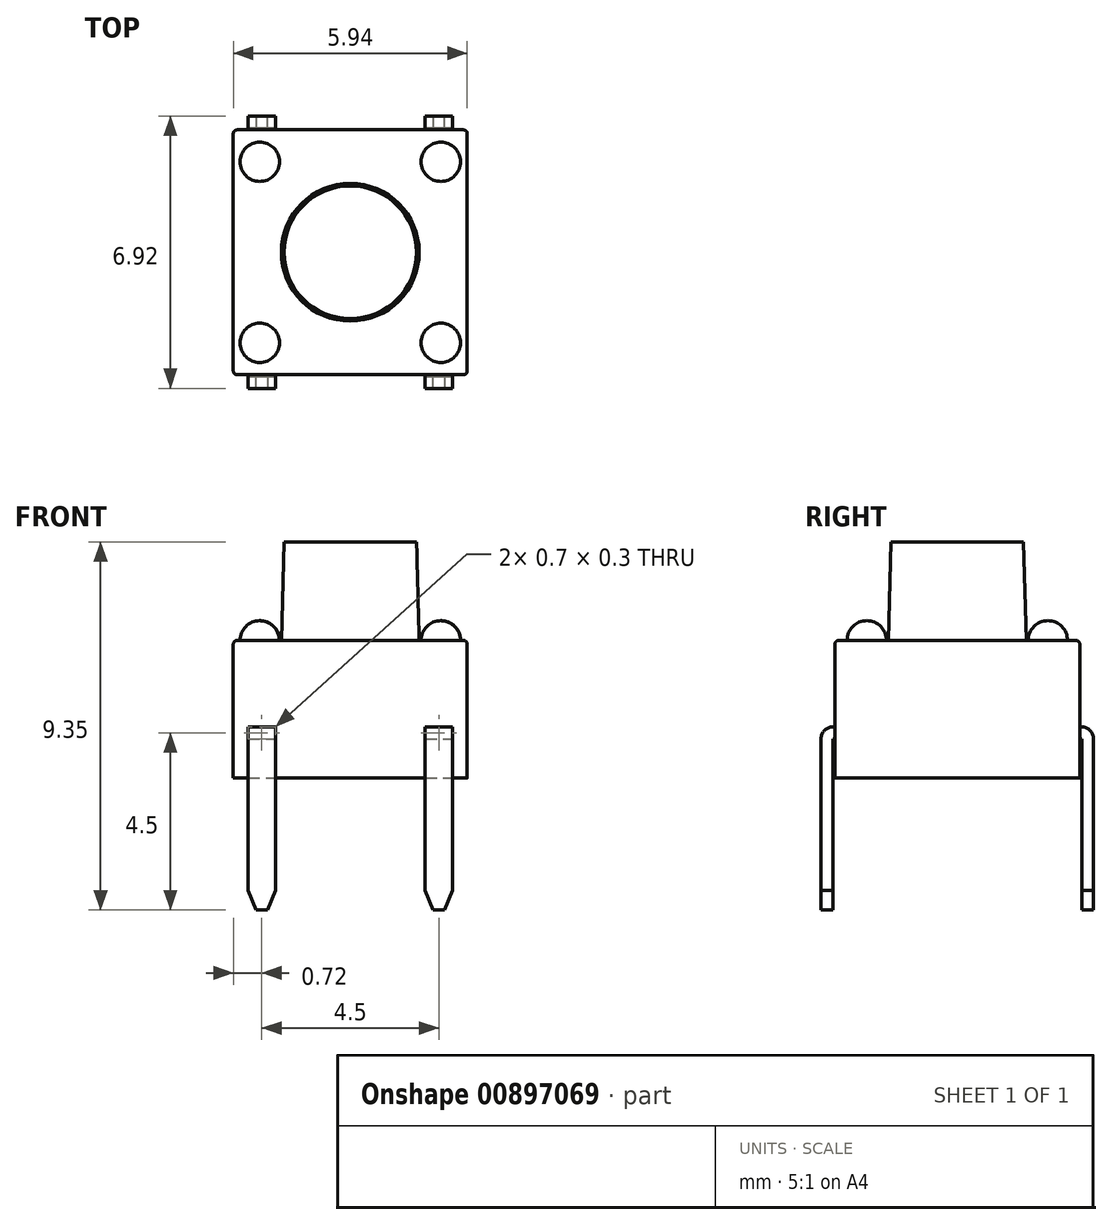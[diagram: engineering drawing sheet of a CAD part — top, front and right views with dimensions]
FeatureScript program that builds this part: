
annotation { "Feature Type Name" : "Feature", "Feature Type Description" : "" }
export const myFeature = defineFeature(function(context is Context, id is Id, definition is map)
    precondition{}
    {
        {
            var Q0;
            Q0=qCreatedBy(makeId("Top.planeOp"),FACE);
            var sketch = newSketch(context, id + "F0", { "sketchPlane" : qUnion([Q0])});
            skLineSegment(sketch, "E0.bottom", {"start": v(-2.97, 3.11) * mm, "end": v(2.97, 3.11) * mm});
            skLineSegment(sketch, "E0.top", {"start": v(-2.97, -3.11) * mm, "end": v(2.97, -3.11) * mm});
            skLineSegment(sketch, "E0.left", {"start": v(-2.97, 3.11) * mm, "end": v(-2.97, -3.11) * mm});
            skLineSegment(sketch, "E0.right", {"start": v(2.97, 3.11) * mm, "end": v(2.97, -3.11) * mm});
            skSolve(sketch);
        }
        {
            var Q0;
            Q0=makeQuery(id+"F0.imprint","IMPRINT",FACE,{"disambiguationData":[TD([[makeQuery(id+"F0.imprint","IMPRINT",EDGE,{"derivedFrom":sQuery(id+"F0.wireOp",EDGE,"E0.bottom")}),-1.0]])]});
            extrude(context, id + "F1", {"entities" : qUnion([Q0]), "depth" : 3.5 * mm});
        }
        {
            var Q0;
            Q0=makeQuery(id+"F1.opExtrude","CAP_FACE",FACE,{"disambiguationData":[OSD([sQuery(id+"F0.wireOp",EDGE,"E0.bottom"),sQuery(id+"F0.wireOp",EDGE,"E0.top"),sQuery(id+"F0.wireOp",EDGE,"E0.left"),sQuery(id+"F0.wireOp",EDGE,"E0.right")])],"isStart":false});
            var sketch = newSketch(context, id + "F2", { "sketchPlane" : qUnion([Q0])});
            skCircle(sketch, "E1", {"center": v(0, 0) * mm, "radius": 1.75 * mm});
            skSolve(sketch);
        }
        {
            var Q0;
            Q0=qSketchRegion(id+"F2",true);
            extrude(context, id + "F3", {"entities" : qUnion([Q0]), "operationType" : NewBodyOperationType.ADD, "offsetDistance" : 25 * mm, "depth" : 2.5 * mm, "hasDraft" : true, "draftAngle" : 1.5 * degree, "draftPullDirection" : true});
        }
        {
            var Q0;
            Q0=makeQuery(id+"F1.opExtrude","SWEPT_EDGE",EDGE,{"disambiguationData":[OSD([sQuery(id+"F0.wireOp",EDGE,"E0.top"),sQuery(id+"F0.wireOp",EDGE,"E0.right")])]});
            var Q1;
            Q1=makeQuery(id+"F1.opExtrude","SWEPT_EDGE",EDGE,{"disambiguationData":[OSD([sQuery(id+"F0.wireOp",EDGE,"E0.top"),sQuery(id+"F0.wireOp",EDGE,"E0.left")])]});
            var Q2;
            Q2=makeQuery(id+"F1.opExtrude","SWEPT_EDGE",EDGE,{"disambiguationData":[OSD([sQuery(id+"F0.wireOp",EDGE,"E0.bottom"),sQuery(id+"F0.wireOp",EDGE,"E0.left")])]});
            var Q3;
            Q3=makeQuery(id+"F1.opExtrude","SWEPT_EDGE",EDGE,{"disambiguationData":[OSD([sQuery(id+"F0.wireOp",EDGE,"E0.bottom"),sQuery(id+"F0.wireOp",EDGE,"E0.right")])]});
            var Q4;
            Q4=makeQuery(id+"F1.opExtrude","CAP_EDGE",EDGE,{"disambiguationData":[OSD([sQuery(id+"F0.wireOp",EDGE,"E0.right")])],"isStart":false});
            var Q5;
            Q5=makeQuery(id+"F1.opExtrude","CAP_EDGE",EDGE,{"disambiguationData":[OSD([sQuery(id+"F0.wireOp",EDGE,"E0.top")])],"isStart":false});
            var Q6;
            Q6=makeQuery(id+"F1.opExtrude","CAP_EDGE",EDGE,{"disambiguationData":[OSD([sQuery(id+"F0.wireOp",EDGE,"E0.left")])],"isStart":false});
            var Q7;
            Q7=makeQuery(id+"F1.opExtrude","CAP_EDGE",EDGE,{"disambiguationData":[OSD([sQuery(id+"F0.wireOp",EDGE,"E0.bottom")])],"isStart":false});
            fillet(context, id + "F4", {"entities" : qUnion([Q0, Q1, Q2, Q3, Q4, Q5, Q6, Q7]), "radius" : 0.1 * mm, "tangentPropagation" : true, "allowEdgeOverflow" : false});
        }
        {
            var Q0;
            Q0=makeQuery(id+"F1.opExtrude","CAP_FACE",FACE,{"disambiguationData":[OSD([sQuery(id+"F0.wireOp",EDGE,"E0.bottom"),sQuery(id+"F0.wireOp",EDGE,"E0.top"),sQuery(id+"F0.wireOp",EDGE,"E0.left"),sQuery(id+"F0.wireOp",EDGE,"E0.right")])],"isStart":false});
            var sketch = newSketch(context, id + "F5", { "sketchPlane" : qUnion([Q0])});
            skCircle(sketch, "E2", {"center": v(2.3, 2.3) * mm, "radius": 0.5 * mm});
            skCircle(sketch, "E3", {"center": v(2.3, -2.3) * mm, "radius": 0.5 * mm});
            skCircle(sketch, "E4", {"center": v(-2.3, -2.3) * mm, "radius": 0.5 * mm});
            skCircle(sketch, "E5", {"center": v(-2.3, 2.3) * mm, "radius": 0.5 * mm});
            skLineSegment(sketch, "E6", {"start": v(0, -3.01) * mm, "end": v(0, 3.01) * mm, "construction": true});
            skLineSegment(sketch, "E7", {"start": v(2.87, 0) * mm, "end": v(-2.87, 0) * mm, "construction": true});
            skSolve(sketch);
        }
        {
            var Q0;
            Q0=makeQuery(id+"F5.imprint","IMPRINT",FACE,{"disambiguationData":[TD([[makeQuery(id+"F5.imprint","IMPRINT",EDGE,{"derivedFrom":sQuery(id+"F5.wireOp",EDGE,"E3")}),1.0]])]});
            var Q1;
            Q1=makeQuery(id+"F5.imprint","IMPRINT",FACE,{"disambiguationData":[TD([[makeQuery(id+"F5.imprint","IMPRINT",EDGE,{"derivedFrom":sQuery(id+"F5.wireOp",EDGE,"E2")}),1.0]])]});
            var Q2;
            Q2=makeQuery(id+"F5.imprint","IMPRINT",FACE,{"disambiguationData":[TD([[makeQuery(id+"F5.imprint","IMPRINT",EDGE,{"derivedFrom":sQuery(id+"F5.wireOp",EDGE,"E5")}),1.0]])]});
            var Q3;
            Q3=makeQuery(id+"F5.imprint","IMPRINT",FACE,{"disambiguationData":[TD([[makeQuery(id+"F5.imprint","IMPRINT",EDGE,{"derivedFrom":sQuery(id+"F5.wireOp",EDGE,"E4")}),1.0]])]});
            extrude(context, id + "F6", {"entities" : qUnion([Q0, Q1, Q2, Q3]), "operationType" : NewBodyOperationType.ADD, "offsetDistance" : 25 * mm, "depth" : 0.5 * mm});
        }
        {
            var Q0;
            Q0=makeQuery(id+"F6.opExtrude","CAP_EDGE",EDGE,{"disambiguationData":[OSD([sQuery(id+"F5.wireOp",EDGE,"E3")])],"isStart":false});
            var Q1;
            Q1=makeQuery(id+"F6.opExtrude","CAP_EDGE",EDGE,{"disambiguationData":[OSD([sQuery(id+"F5.wireOp",EDGE,"E2")])],"isStart":false});
            var Q2;
            Q2=makeQuery(id+"F6.opExtrude","CAP_EDGE",EDGE,{"disambiguationData":[OSD([sQuery(id+"F5.wireOp",EDGE,"E5")])],"isStart":false});
            var Q3;
            Q3=makeQuery(id+"F6.opExtrude","CAP_EDGE",EDGE,{"disambiguationData":[OSD([sQuery(id+"F5.wireOp",EDGE,"E4")])],"isStart":false});
            fillet(context, id + "F7", {"entities" : qUnion([Q0, Q1, Q2, Q3]), "radius" : 0.5 * mm, "tangentPropagation" : true, "allowEdgeOverflow" : false});
        }
        {
            var Q0;
            Q0=makeQuery(id+"F1.opExtrude","SWEPT_FACE",FACE,{"disambiguationData":[OSD([sQuery(id+"F0.wireOp",EDGE,"E0.top")])]});
            var sketch = newSketch(context, id + "F8", { "sketchPlane" : qUnion([Q0])});
            skLineSegment(sketch, "E8.bottom", {"start": v(-2.6, 1.3) * mm, "end": v(-1.9, 1.3) * mm});
            skLineSegment(sketch, "E8.top", {"start": v(-2.6, 1) * mm, "end": v(-1.9, 1) * mm});
            skLineSegment(sketch, "E8.left", {"start": v(-2.6, 1.3) * mm, "end": v(-2.6, 1) * mm});
            skLineSegment(sketch, "E8.right", {"start": v(-1.9, 1.3) * mm, "end": v(-1.9, 1) * mm});
            skLineSegment(sketch, "E9.bottom", {"start": v(1.9, 1.3) * mm, "end": v(2.6, 1.3) * mm});
            skLineSegment(sketch, "E9.top", {"start": v(1.9, 1) * mm, "end": v(2.6, 1) * mm});
            skLineSegment(sketch, "E9.left", {"start": v(1.9, 1.3) * mm, "end": v(1.9, 1) * mm});
            skLineSegment(sketch, "E9.right", {"start": v(2.6, 1.3) * mm, "end": v(2.6, 1) * mm});
            skLineSegment(sketch, "E10", {"start": v(0, 3.4) * mm, "end": v(0, 0) * mm, "construction": true});
            skSolve(sketch);
        }
        {
            var Q0;
            Q0=qCreatedBy(makeId("Right.planeOp"),FACE);
            var sketch = newSketch(context, id + "F9", { "sketchPlane" : qUnion([Q0])});
            skLineSegment(sketch, "E11", {"start": v(-3.11, 1.15) * mm, "end": v(-3.16, 1.15) * mm});
            skLineSegment(sketch, "E12", {"start": v(-3.11, 1.58) * mm, "end": v(-3.11, 0.7) * mm, "construction": true});
            skLineSegment(sketch, "E13", {"start": v(-3.31, 1) * mm, "end": v(-3.31, -3.35) * mm});
            skPoint(sketch, "E14.visualSharp", {"position": v(-3.31, 1.15) * mm});
            skArc(sketch, "E14.filletArc", {"start": v(-3.16, 1.15) * mm, "mid": v(-3.27, 1.1) * mm, "end": v(-3.31, 1) * mm});
            skSolve(sketch);
        }
        {
            var Q0;
            Q0=makeQuery(id+"F8.imprint","IMPRINT",FACE,{"disambiguationData":[TD([[makeQuery(id+"F8.imprint","IMPRINT",EDGE,{"derivedFrom":sQuery(id+"F8.wireOp",EDGE,"E8.bottom")}),-1.0]])]});
            var Q1;
            Q1=makeQuery(id+"F8.imprint","IMPRINT",FACE,{"disambiguationData":[TD([[makeQuery(id+"F8.imprint","IMPRINT",EDGE,{"derivedFrom":sQuery(id+"F8.wireOp",EDGE,"E9.bottom")}),-1.0]])]});
            var Q2;
            Q2=sQuery(id+"F9.wireOp",EDGE,"E11");
            var Q3;
            Q3=sQuery(id+"F9.wireOp",EDGE,"E14.filletArc");
            var Q4;
            Q4=sQuery(id+"F9.wireOp",EDGE,"E13");
            sweep(context, id + "F10", {"profiles" : qUnion([Q0, Q1]), "path" : qUnion([Q2, Q3, Q4])});
        }
        {
            var Q0;
            Q0=makeQuery(id+"F10.opSweep","CAP_EDGE",EDGE,{"disambiguationData":[OSD([sQuery(id+"F8.wireOp",EDGE,"E8.left"),sQuery(id+"F9.wireOp",VERTEX,"E13.end")])],"isStart":false});
            var Q1;
            Q1=makeQuery(id+"F10.opSweep","CAP_EDGE",EDGE,{"disambiguationData":[OSD([sQuery(id+"F8.wireOp",EDGE,"E8.right"),sQuery(id+"F9.wireOp",VERTEX,"E13.end")])],"isStart":false});
            var Q2;
            Q2=makeQuery(id+"F10.opSweep","CAP_EDGE",EDGE,{"disambiguationData":[OSD([sQuery(id+"F8.wireOp",EDGE,"E9.left"),sQuery(id+"F9.wireOp",VERTEX,"E13.end")])],"isStart":false});
            var Q3;
            Q3=makeQuery(id+"F10.opSweep","CAP_EDGE",EDGE,{"disambiguationData":[OSD([sQuery(id+"F8.wireOp",EDGE,"E9.right"),sQuery(id+"F9.wireOp",VERTEX,"E13.end")])],"isStart":false});
            chamfer(context, id + "F11", {"entities" : qUnion([Q0, Q1, Q2, Q3]), "chamferType" : ChamferType.TWO_OFFSETS, "width1" : 0.2 * mm, "oppositeDirection" : false, "width2" : 0.5 * mm, "tangentPropagation" : true});
        }
        {
            var Q0;
            Q0=makeQuery(id+"F10.opSweep","SWEPT_BODY",BODY,{"disambiguationData":[OSD([sQuery(id+"F8.wireOp",EDGE,"E9.bottom"),sQuery(id+"F8.wireOp",EDGE,"E9.top"),sQuery(id+"F8.wireOp",EDGE,"E9.left"),sQuery(id+"F8.wireOp",EDGE,"E9.right"),sQuery(id+"F9.wireOp",EDGE,"E13")])]});
            var Q1;
            Q1=makeQuery(id+"F10.opSweep","SWEPT_BODY",BODY,{"disambiguationData":[OSD([sQuery(id+"F8.wireOp",EDGE,"E8.bottom"),sQuery(id+"F8.wireOp",EDGE,"E8.top"),sQuery(id+"F8.wireOp",EDGE,"E8.left"),sQuery(id+"F8.wireOp",EDGE,"E8.right"),sQuery(id+"F9.wireOp",EDGE,"E13")])]});
            var Q2;
            Q2=qCreatedBy(makeId("Front.planeOp"),FACE);
            mirror(context, id + "F12", {"operationType" : NewBodyOperationType.ADD, "entities" : qUnion([Q0, Q1]), "mirrorPlane" : qUnion([Q2])});
        }
    });
